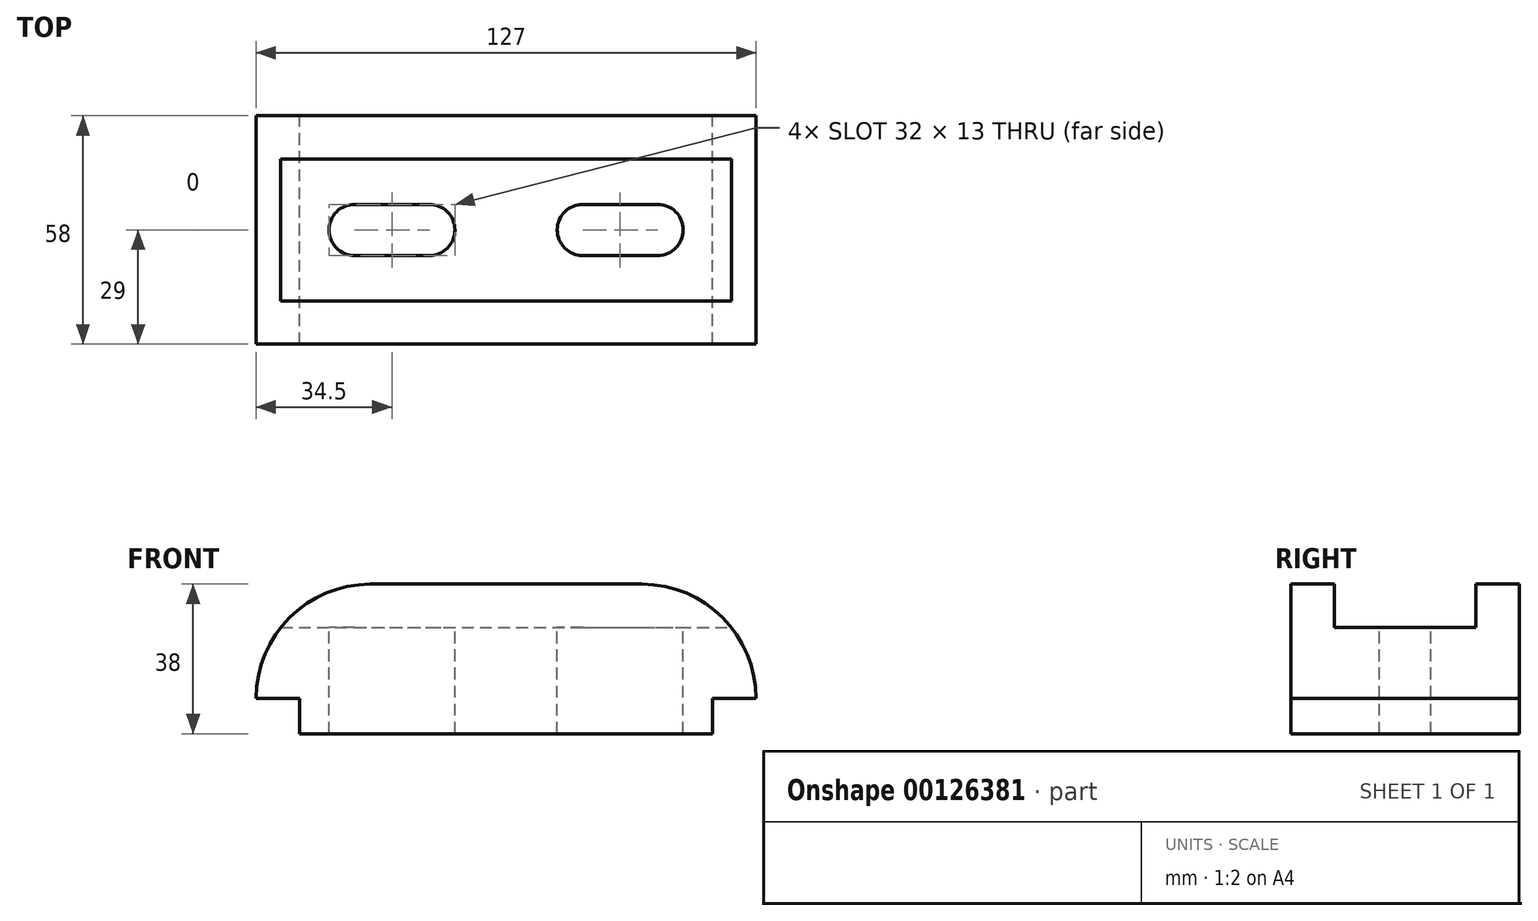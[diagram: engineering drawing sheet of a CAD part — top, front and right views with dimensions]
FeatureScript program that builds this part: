
annotation { "Feature Type Name" : "Feature", "Feature Type Description" : "" }
export const myFeature = defineFeature(function(context is Context, id is Id, definition is map)
    precondition{}
    {
        {
            var Q0;
            Q0=qCreatedBy(makeId("Front.planeOp"),FACE);
            var sketch = newSketch(context, id + "F0", { "sketchPlane" : qUnion([Q0])});
            skLineSegment(sketch, "E0", {"start": v(0, 0) * mm, "end": v(0, 9) * mm});
            skLineSegment(sketch, "E1", {"start": v(0, 0) * mm, "end": v(105, 0) * mm});
            skLineSegment(sketch, "E2", {"start": v(105, 0) * mm, "end": v(105, 9) * mm});
            skLineSegment(sketch, "E3", {"start": v(0, 9) * mm, "end": v(-11, 9) * mm});
            skLineSegment(sketch, "E4", {"start": v(105, 9) * mm, "end": v(116, 9) * mm});
            skLineSegment(sketch, "E5", {"start": v(18, 38) * mm, "end": v(87, 38) * mm});
            skArc(sketch, "E6", {"start": v(18, 38) * mm, "mid": v(-2.5, 29.5) * mm, "end": v(-11, 9) * mm});
            skArc(sketch, "E7", {"start": v(116, 9) * mm, "mid": v(107.5, 29.5) * mm, "end": v(87, 38) * mm});
            skSolve(sketch);
        }
        {
            var Q0;
            Q0=makeQuery(id+"F0.imprint","IMPRINT",FACE,{"disambiguationData":[TD([[makeQuery(id+"F0.imprint","IMPRINT",EDGE,{"derivedFrom":sQuery(id+"F0.wireOp",EDGE,"E0")}),-1.0]])]});
            extrude(context, id + "F1", {"entities" : qUnion([Q0]), "endBound" : BoundingType.SYMMETRIC, "depth" : 58 * mm});
        }
        {
            var Q0;
            Q0=makeQuery(id+"F1.opExtrude","SWEPT_FACE",FACE,{"disambiguationData":[OSD([sQuery(id+"F0.wireOp",EDGE,"E5")])]});
            cPlane(context, id + "F2", {"entities" : qUnion([Q0]), "cplaneType" : CPlaneType.OFFSET, "offset" : 0 * mm, "width" : 150 * mm, "height" : 150 * mm});
        }
        {
            var Q0;
            Q0=qCreatedBy(id+"F2.planeOp",FACE);
            var sketch = newSketch(context, id + "F3", { "sketchPlane" : qUnion([Q0])});
            skLineSegment(sketch, "E8", {"start": v(-47.95, 0) * mm, "end": v(152.47, 0) * mm, "construction": true});
            skLineSegment(sketch, "E9", {"start": v(-11, 18) * mm, "end": v(-11, -18) * mm});
            skLineSegment(sketch, "E10", {"start": v(-11, 18) * mm, "end": v(116, 18) * mm});
            skLineSegment(sketch, "E11", {"start": v(-11, -18) * mm, "end": v(116, -18) * mm});
            skLineSegment(sketch, "E12", {"start": v(116, 18) * mm, "end": v(116, -18) * mm});
            skLineSegment(sketch, "E13", {"start": v(14, 6.5) * mm, "end": v(33, 6.5) * mm});
            skLineSegment(sketch, "E14", {"start": v(14, -6.5) * mm, "end": v(33, -6.5) * mm});
            skLineSegment(sketch, "E15", {"start": v(72, 6.5) * mm, "end": v(91, 6.5) * mm});
            skLineSegment(sketch, "E16", {"start": v(72, -6.5) * mm, "end": v(91, -6.5) * mm});
            skArc(sketch, "E17", {"start": v(14, 6.5) * mm, "mid": v(7.5, 0) * mm, "end": v(14, -6.5) * mm});
            skArc(sketch, "E18", {"start": v(33, 6.5) * mm, "mid": v(39.5, 0) * mm, "end": v(33, -6.5) * mm});
            skArc(sketch, "E19", {"start": v(72, 6.5) * mm, "mid": v(65.5, 0) * mm, "end": v(72, -6.5) * mm});
            skArc(sketch, "E20", {"start": v(91, 6.5) * mm, "mid": v(97.5, 0) * mm, "end": v(91, -6.5) * mm});
            skSolve(sketch);
        }
        {
            var Q0;
            Q0=makeQuery(id+"F3.imprint","IMPRINT",FACE,{"disambiguationData":[TD([[makeQuery(id+"F3.imprint","IMPRINT",EDGE,{"derivedFrom":sQuery(id+"F3.wireOp",EDGE,"E9")}),1.0]])]});
            extrude(context, id + "F4", {"entities" : qUnion([Q0]), "operationType" : NewBodyOperationType.REMOVE, "oppositeDirection" : true, "depth" : 11 * mm});
        }
        {
            var Q0;
            Q0=makeQuery(id+"F3.imprint","IMPRINT",FACE,{"disambiguationData":[TD([[makeQuery(id+"F3.imprint","IMPRINT",EDGE,{"derivedFrom":sQuery(id+"F3.wireOp",EDGE,"E13")}),-1.0]])]});
            var Q1;
            Q1=makeQuery(id+"F3.imprint","IMPRINT",FACE,{"disambiguationData":[TD([[makeQuery(id+"F3.imprint","IMPRINT",EDGE,{"derivedFrom":sQuery(id+"F3.wireOp",EDGE,"E15")}),-1.0]])]});
            extrude(context, id + "F5", {"entities" : qUnion([Q0, Q1]), "operationType" : NewBodyOperationType.REMOVE, "endBound" : BoundingType.THROUGH_ALL, "oppositeDirection" : true, "depth" : 25 * mm});
        }
    });
